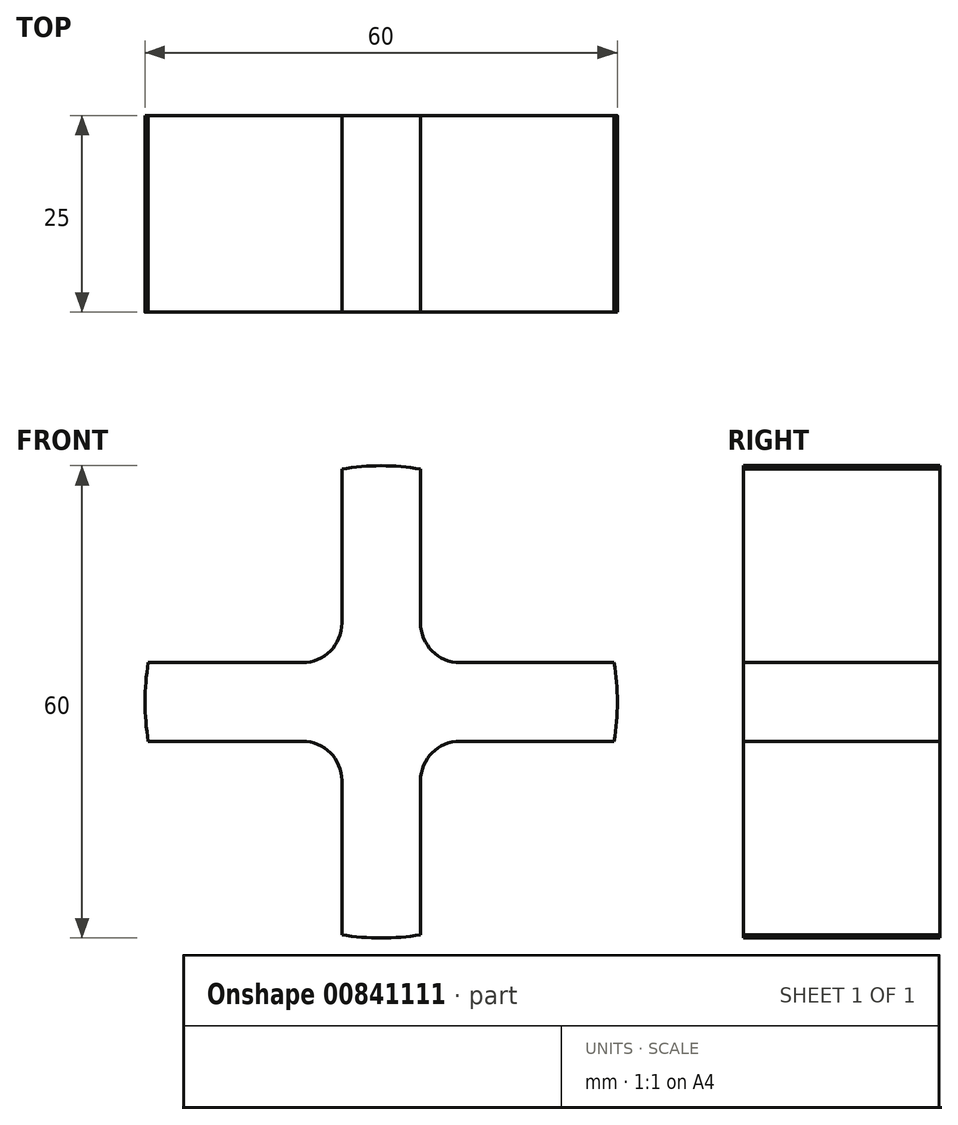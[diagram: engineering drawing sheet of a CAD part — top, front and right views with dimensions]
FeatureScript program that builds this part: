
annotation { "Feature Type Name" : "Feature", "Feature Type Description" : "" }
export const myFeature = defineFeature(function(context is Context, id is Id, definition is map)
    precondition{}
    {
        {
            var Q0;
            Q0=qCreatedBy(makeId("Front.planeOp"),FACE);
            var sketch = newSketch(context, id + "F0", { "sketchPlane" : qUnion([Q0])});
            skArc(sketch, "E0", {"start": v(5, 29.58) * mm, "mid": v(0, 30) * mm, "end": v(-5, 29.58) * mm});
            skLineSegment(sketch, "E1", {"start": v(-5, 5) * mm, "end": v(-5, 29.58) * mm});
            skLineSegment(sketch, "E2", {"start": v(-5, 35) * mm, "end": v(-35, 35) * mm, "construction": true});
            skLineSegment(sketch, "E3", {"start": v(-35, 35) * mm, "end": v(-35, 5) * mm, "construction": true});
            skLineSegment(sketch, "E4", {"start": v(-29.58, 5) * mm, "end": v(-5, 5) * mm});
            skLineSegment(sketch, "E5", {"start": v(0, 0) * mm, "end": v(-45.02, 45.02) * mm, "construction": true});
            skLineSegment(sketch, "E6.MirrorCS", {"start": v(5, 5) * mm, "end": v(5, 29.58) * mm});
            skLineSegment(sketch, "E7.MirrorCS", {"start": v(29.58, 5) * mm, "end": v(5, 5) * mm});
            skLineSegment(sketch, "E8.MirrorCS", {"start": v(-29.58, -5) * mm, "end": v(-5, -5) * mm});
            skLineSegment(sketch, "E9.MirrorCS", {"start": v(-5, -5) * mm, "end": v(-5, -29.58) * mm});
            skLineSegment(sketch, "E10.MirrorCS", {"start": v(5, -5) * mm, "end": v(5, -29.58) * mm});
            skLineSegment(sketch, "E11.MirrorCS", {"start": v(29.58, -5) * mm, "end": v(5, -5) * mm});
            skArc(sketch, "E12.trimOffspring", {"start": v(29.58, -5) * mm, "mid": v(30, 0) * mm, "end": v(29.58, 5) * mm});
            skArc(sketch, "E13.trimOffspring", {"start": v(-5, -29.58) * mm, "mid": v(0, -30) * mm, "end": v(5, -29.58) * mm});
            skArc(sketch, "E14.trimOffspring", {"start": v(-29.58, 5) * mm, "mid": v(-30, 0) * mm, "end": v(-29.58, -5) * mm});
            skSolve(sketch);
        }
        {
            var Q0;
            Q0=makeQuery(id+"F0.imprint","IMPRINT",FACE,{"disambiguationData":[TD([[makeQuery(id+"F0.imprint","IMPRINT",EDGE,{"derivedFrom":sQuery(id+"F0.wireOp",EDGE,"E0")}),1.0]])]});
            extrude(context, id + "F1", {"entities" : qUnion([Q0]), "depth" : 25 * mm, "offsetDistance" : 25 * mm});
        }
        {
            var Q0;
            Q0=makeQuery(id+"F1.opExtrude","SWEPT_EDGE",EDGE,{"disambiguationData":[OSD([sQuery(id+"F0.wireOp",EDGE,"E1"),sQuery(id+"F0.wireOp",EDGE,"E4")])]});
            var Q1;
            Q1=makeQuery(id+"F1.opExtrude","SWEPT_EDGE",EDGE,{"disambiguationData":[OSD([sQuery(id+"F0.wireOp",EDGE,"E6.MirrorCS"),sQuery(id+"F0.wireOp",EDGE,"E7.MirrorCS")])]});
            var Q2;
            Q2=makeQuery(id+"F1.opExtrude","SWEPT_EDGE",EDGE,{"disambiguationData":[OSD([sQuery(id+"F0.wireOp",EDGE,"E8.MirrorCS"),sQuery(id+"F0.wireOp",EDGE,"E9.MirrorCS")])]});
            var Q3;
            Q3=makeQuery(id+"F1.opExtrude","SWEPT_EDGE",EDGE,{"disambiguationData":[OSD([sQuery(id+"F0.wireOp",EDGE,"E10.MirrorCS"),sQuery(id+"F0.wireOp",EDGE,"E11.MirrorCS")])]});
            fillet(context, id + "F2", {"entities" : qUnion([Q0, Q1, Q2, Q3]), "radius" : 5 * mm, "tangentPropagation" : true, "allowEdgeOverflow" : false});
        }
    });
